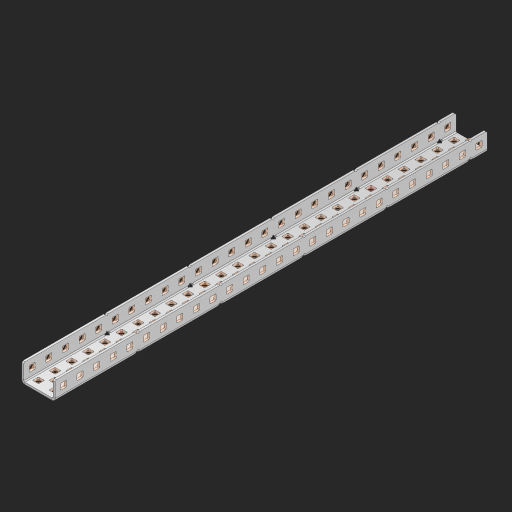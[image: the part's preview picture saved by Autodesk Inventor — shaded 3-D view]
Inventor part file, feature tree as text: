
AUTODESK INVENTOR PART (.ipt)
format: ipt  version: 2023 (Build 270158000, 158)  size: 1,687,552 bytes
history: native  units: in
note: dims shown in document units (in); Inventor stores cm internally (conversion verified against a paired STEP export)
features: other x137, extrude x128, sheet_metal_op x11, sketch x10, pattern_linear x2, mirror x1, chamfer x1
ambient origin geometry x8: Origin, YZ Plane, XZ Plane, XY Plane, X Axis, Y Axis, Z Axis, Center Point
bodies: Solid1 (feature_tree), Body (feature_tree)
feature tree (290):
  sheet_metal_op  "Flanges"
  other  "Flange Pattern Plane"
  other  "Flange Pattern Sketch"
  sheet_metal_op  "Flange Pattern"
  sheet_metal_op  "Body Pattern"
  pattern_linear  "Center Pattern"  Spacing1=0.0625in  [1 undecoded]
  other  "Arc Length"
  mirror  "Notch Mirror"
  pattern_linear  "Notch Pattern"  Spacing1=0.182in  [1 undecoded]
  chamfer  "End Chamfer"
  extrude  "Half Cut"  Depth=0.02in
  sketch  "Sketch1"  dims[d0=1.0in]
  other  "Plate1"
  sketch  "Sketch2"  dims[d1=13.0in]
  other  "Plate2"
  sheet_metal_op  "Bend1"
  sheet_metal_op  "Corner1"
  sketch  "Sketch3"  dims[d2=0.0625in]
  sketch  "Sketch7"  dims[d3=0.0625in]
  other  "Srf1"
  other  "Srf2"
  sketch  "Sketch8"  dims[d4=0.0312in]
  sketch  "Sketch9"  dims[d5=0.125in]
  other  "Srf91"
  sheet_metal_op  "Body Pattern Sketch"
  other  "Srf92"
  sketch  "Sketch13"  dims[d6=0.0625in]
  sketch  "Sketch14"  dims[d7=0.5in d8=90.0deg d9=0.0312in]
  sketch  "Sketch15"  dims[d10=0.25in]
  sketch  "Sketch16"  dims[d11=0.0625in d12=0.0625in d16=0.182in d17=0.02in d18=0.0625in d19=0.0in d20=0.25in d21=0.25in d38=10.2362in d40=0.5in d41=0.7874in d43=1.0in d46=0.172in d47=1.0in d48=0.0in d49=0.182in d50=0.02in d51=0.25in d52=0.25in d53=0.0625in d54=0.0in d55=0.172in d56=1.0in d57=0.0in d58=0.25in d60=10.2362in d62=0.5in d63=0.7874in d65=0.5in d85=0.1473in d86=0.1782in d88=0.04in d89=0.0625in d90=0.0in d91=0.04in d92=0.0491in d95=2.5in d96=0.04in d97=0.25in d98=45.0deg d99=0.25in d100=0.5in d101=0.0in d102=2.497in d106=0.182in d107=0.02in d108=0.5in d109=0.5in d110=0.0625in d111=0.0in d112=0.172in d113=0.5in d114=0.0in d117=0.5in d118=0.5in d119=0.5in]
  other  "Srf786"
  other  "Srf823"
  other  "Srf824"
  other  "Srf825"
  other  "Srf826"
  other  "Srf827"
  other  "Srf828"
  other  "Srf829"
  other  "Srf856"
  other  "Srf857"
  other  "Srf858"
  other  "Srf859"
  other  "Srf860"
  other  "Srf861"
  other  "Srf862"
  other  "Srf889"
  other  "Srf890"
  other  "Srf891"
  other  "Srf892"
  other  "Srf893"
  other  "Srf894"
  other  "Srf895"
  other  "Srf896"
  other  "Srf922"
  other  "Srf923"
  other  "Srf924"
  other  "Srf925"
  other  "Srf926"
  other  "Srf959"
  other  "Srf960"
  other  "Srf961"
  other  "Srf962"
  other  "Srf963"
  other  "Srf996"
  other  "Srf997"
  other  "Srf998"
  other  "Srf999"
  other  "Srf1000"
  other  "Srf1143"
  other  "Srf1144"
  other  "Srf1145"
  other  "Srf1146"
  other  "Srf1147"
  other  "Srf1148"
  other  "Srf1149"
  other  "Srf1150"
  other  "Srf1151"
  other  "Srf1152"
  other  "Srf1153"
  other  "Srf1154"
  other  "Srf1155"
  other  "Srf1156"
  other  "Srf1157"
  other  "Srf1158"
  other  "Srf1159"
  other  "Srf1160"
  other  "Srf1161"
  other  "Srf1162"
  other  "Srf1163"
  other  "Srf1164"
  other  "Srf1165"
  other  "Srf1166"
  other  "Srf1167"
  other  "Srf1168"
  other  "Srf1169"
  other  "Srf1170"
  other  "Srf1171"
  other  "Srf1172"
  other  "Srf1173"
  other  "Srf1174"
  other  "Srf1175"
  other  "Srf1176"
  other  "Srf1177"
  other  "Srf1178"
  other  "Srf1179"
  other  "Srf1180"
  other  "Srf1199"
  other  "Srf1200"
  other  "Srf1201"
  other  "Srf1202"
  other  "Srf1203"
  other  "Srf1204"
  other  "Srf1205"
  other  "Srf1206"
  other  "Srf1207"
  other  "Srf1208"
  other  "Srf1209"
  other  "Srf1210"
  other  "Srf1211"
  other  "Srf1212"
  other  "Srf1213"
  other  "Srf1214"
  other  "Srf1215"
  other  "Srf1216"
  other  "Srf1217"
  other  "Srf1218"
  other  "Srf1219"
  other  "Srf1220"
  other  "Srf1221"
  other  "Srf1222"
  other  "Srf1223"
  other  "Srf1224"
  other  "Srf1225"
  other  "Srf1226"
  other  "Srf1227"
  other  "Srf1228"
  other  "Srf1229"
  other  "Srf1230"
  other  "Srf1231"
  other  "Srf1232"
  other  "Srf1233"
  other  "Srf1234"
  other  "Srf1235"
  other  "Srf1236"
  other  "Srf1255"
  other  "Srf1256"
  other  "Srf1257"
  other  "Srf1258"
  other  "Srf1259"
  other  "Srf1260"
  other  "Srf1261"
  other  "Srf1262"
  other  "Srf1263"
  other  "Srf1264"
  other  "Srf1265"
  other  "Srf1266"
  sheet_metal_op  "Flange Stamp"
  sheet_metal_op  "Flange Circle"
  sheet_metal_op  "Body Stamp"
  sheet_metal_op  "Body Circle"
  other  "Center Stamp"
  other  "Center Circle"
  sheet_metal_op  "Notch"
  extrude  "ExtrusionSrf2"  Depth=0.0625in
  extrude  "ExtrusionSrf92"  TaperAngle=0.0deg  [1 undecoded]
  extrude  "ExtrusionSrf823"  Depth=0.5in
  extrude  "ExtrusionSrf824"  Depth=0.5in
  extrude  "ExtrusionSrf825"  Depth=0.5in
  extrude  "ExtrusionSrf826"  Depth=0.5in
  extrude  "ExtrusionSrf827"  Depth=1.0in TaperAngle=0.0deg
  extrude  "ExtrusionSrf828"  Depth=0.5in
  extrude  "ExtrusionSrf829"  Depth=0.02in
  extrude  "ExtrusionSrf856"  Depth=0.5in
  extrude  "ExtrusionSrf857"  Depth=0.5in
  extrude  "ExtrusionSrf858"  Depth=0.0625in
  extrude  "ExtrusionSrf859"  TaperAngle=0.0deg  [1 undecoded]
  extrude  "ExtrusionSrf860"  Depth=0.5in
  extrude  "ExtrusionSrf861"  Depth=1.0in TaperAngle=0.0deg
  extrude  "ExtrusionSrf862"  Depth=0.5in
  extrude  "ExtrusionSrf889"  Depth=0.5in
  extrude  "ExtrusionSrf890"  Depth=0.5in
  extrude  "ExtrusionSrf891"  Depth=0.5in
  extrude  "ExtrusionSrf892"  Depth=0.5in
  extrude  "ExtrusionSrf893"  Depth=0.5in
  extrude  "ExtrusionSrf894"  Depth=0.0625in
  extrude  "ExtrusionSrf895"  TaperAngle=0.0deg  [1 undecoded]
  extrude  "ExtrusionSrf896"  Depth=0.5in
  extrude  "ExtrusionSrf922"  Depth=0.5in
  extrude  "ExtrusionSrf923"  Depth=2.5in
  extrude  "ExtrusionSrf924"  Depth=0.5in TaperAngle=45.0deg
  extrude  "ExtrusionSrf925"  Depth=0.5in
  extrude  "ExtrusionSrf926"  Depth=0.5in TaperAngle=0.0deg
  extrude  "ExtrusionSrf959"  Depth=0.5in
  extrude  "ExtrusionSrf960"  Depth=0.5in
  extrude  "ExtrusionSrf961"  Depth=0.02in
  extrude  "ExtrusionSrf962"  Depth=0.5in
  extrude  "ExtrusionSrf963"  Depth=0.5in
  extrude  "ExtrusionSrf996"  Depth=0.0625in
  extrude  "ExtrusionSrf997"  TaperAngle=0.0deg  [1 undecoded]
  extrude  "ExtrusionSrf998"  Depth=0.5in
  extrude  "ExtrusionSrf999"  Depth=0.5in TaperAngle=0.0deg
  extrude  "ExtrusionSrf1000"  Depth=0.5in
  extrude  "ExtrusionSrf1143"  Depth=0.5in
  extrude  "ExtrusionSrf1144"  Depth=0.5in
  extrude  "ExtrusionSrf1145"  [1 undecoded]
  extrude  "ExtrusionSrf1146"  [1 undecoded]
  extrude  "ExtrusionSrf1147"  [1 undecoded]
  extrude  "ExtrusionSrf1148"  [1 undecoded]
  extrude  "ExtrusionSrf1149"  [1 undecoded]
  extrude  "ExtrusionSrf1150"  [1 undecoded]
  extrude  "ExtrusionSrf1151"  [1 undecoded]
  extrude  "ExtrusionSrf1152"  [1 undecoded]
  extrude  "ExtrusionSrf1153"  [1 undecoded]
  extrude  "ExtrusionSrf1154"  [1 undecoded]
  extrude  "ExtrusionSrf1155"  [1 undecoded]
  extrude  "ExtrusionSrf1156"  [1 undecoded]
  extrude  "ExtrusionSrf1157"  [1 undecoded]
  extrude  "ExtrusionSrf1158"  [1 undecoded]
  extrude  "ExtrusionSrf1159"  [1 undecoded]
  extrude  "ExtrusionSrf1160"  [1 undecoded]
  extrude  "ExtrusionSrf1161"  [1 undecoded]
  extrude  "ExtrusionSrf1162"  [1 undecoded]
  extrude  "ExtrusionSrf1163"  [1 undecoded]
  extrude  "ExtrusionSrf1164"  [1 undecoded]
  extrude  "ExtrusionSrf1165"  [1 undecoded]
  extrude  "ExtrusionSrf1166"  [1 undecoded]
  extrude  "ExtrusionSrf1167"  [1 undecoded]
  extrude  "ExtrusionSrf1168"  [1 undecoded]
  extrude  "ExtrusionSrf1169"  [1 undecoded]
  extrude  "ExtrusionSrf1170"  [1 undecoded]
  extrude  "ExtrusionSrf1171"  [1 undecoded]
  extrude  "ExtrusionSrf1172"  [1 undecoded]
  extrude  "ExtrusionSrf1173"  [1 undecoded]
  extrude  "ExtrusionSrf1174"  [1 undecoded]
  extrude  "ExtrusionSrf1175"  [1 undecoded]
  extrude  "ExtrusionSrf1176"  [1 undecoded]
  extrude  "ExtrusionSrf1177"  [1 undecoded]
  extrude  "ExtrusionSrf1178"  [1 undecoded]
  extrude  "ExtrusionSrf1179"  [1 undecoded]
  extrude  "ExtrusionSrf1180"  [1 undecoded]
  extrude  "ExtrusionSrf1199"  [1 undecoded]
  extrude  "ExtrusionSrf1200"  [1 undecoded]
  extrude  "ExtrusionSrf1201"  [1 undecoded]
  extrude  "ExtrusionSrf1202"  [1 undecoded]
  extrude  "ExtrusionSrf1203"  [1 undecoded]
  extrude  "ExtrusionSrf1204"  [1 undecoded]
  extrude  "ExtrusionSrf1205"  [1 undecoded]
  extrude  "ExtrusionSrf1206"  [1 undecoded]
  extrude  "ExtrusionSrf1207"  [1 undecoded]
  extrude  "ExtrusionSrf1208"  [1 undecoded]
  extrude  "ExtrusionSrf1209"  [1 undecoded]
  extrude  "ExtrusionSrf1210"  [1 undecoded]
  extrude  "ExtrusionSrf1211"  [1 undecoded]
  extrude  "ExtrusionSrf1212"  [1 undecoded]
  extrude  "ExtrusionSrf1213"  [1 undecoded]
  extrude  "ExtrusionSrf1214"  [1 undecoded]
  extrude  "ExtrusionSrf1215"  [1 undecoded]
  extrude  "ExtrusionSrf1216"  [1 undecoded]
  extrude  "ExtrusionSrf1217"  [1 undecoded]
  extrude  "ExtrusionSrf1218"  [1 undecoded]
  extrude  "ExtrusionSrf1219"  [1 undecoded]
  extrude  "ExtrusionSrf1220"  [1 undecoded]
  extrude  "ExtrusionSrf1221"  [1 undecoded]
  extrude  "ExtrusionSrf1222"  [1 undecoded]
  extrude  "ExtrusionSrf1223"  [1 undecoded]
  extrude  "ExtrusionSrf1224"  [1 undecoded]
  extrude  "ExtrusionSrf1225"  [1 undecoded]
  extrude  "ExtrusionSrf1226"  [1 undecoded]
  extrude  "ExtrusionSrf1227"  [1 undecoded]
  extrude  "ExtrusionSrf1228"  [1 undecoded]
  extrude  "ExtrusionSrf1229"  [1 undecoded]
  extrude  "ExtrusionSrf1230"  [1 undecoded]
  extrude  "ExtrusionSrf1231"  [1 undecoded]
  extrude  "ExtrusionSrf1232"  [1 undecoded]
  extrude  "ExtrusionSrf1233"  [1 undecoded]
  extrude  "ExtrusionSrf1234"  [1 undecoded]
  extrude  "ExtrusionSrf1235"  [1 undecoded]
  extrude  "ExtrusionSrf1236"  [1 undecoded]
  extrude  "ExtrusionSrf1255"  [1 undecoded]
  extrude  "ExtrusionSrf1256"  [1 undecoded]
  extrude  "ExtrusionSrf1257"  [1 undecoded]
  extrude  "ExtrusionSrf1258"  [1 undecoded]
  extrude  "ExtrusionSrf1259"  [1 undecoded]
  extrude  "ExtrusionSrf1260"  [1 undecoded]
  extrude  "ExtrusionSrf1261"  [1 undecoded]
  extrude  "ExtrusionSrf1262"  [1 undecoded]
  extrude  "ExtrusionSrf1263"  [1 undecoded]
  extrude  "ExtrusionSrf1264"  [1 undecoded]
  extrude  "ExtrusionSrf1265"  [1 undecoded]
  extrude  "ExtrusionSrf1266"  [1 undecoded]
note: 92 required parameter values undecoded (feature->parameter linkage not recoverable at this tier; creation-order binding heuristic only, values carry confidence <= 0.55)
